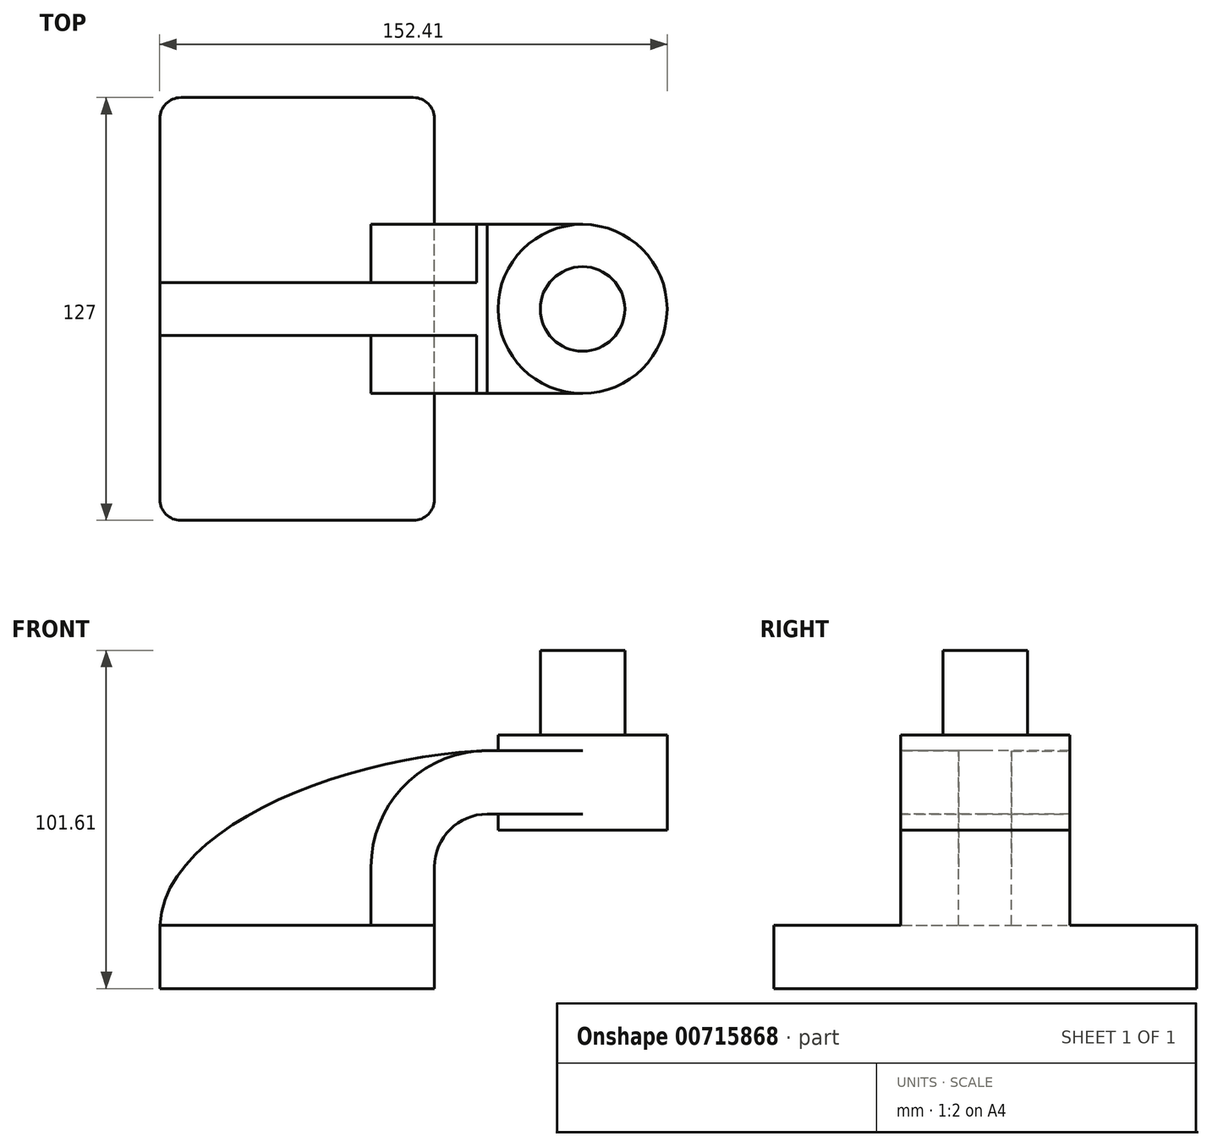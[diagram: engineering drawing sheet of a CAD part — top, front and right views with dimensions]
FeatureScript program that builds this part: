
annotation { "Feature Type Name" : "Feature", "Feature Type Description" : "" }
export const myFeature = defineFeature(function(context is Context, id is Id, definition is map)
    precondition{}
    {
        {
            var Q0;
            Q0=qCreatedBy(makeId("Front.planeOp"),FACE);
            var sketch = newSketch(context, id + "F0", { "sketchPlane" : qUnion([Q0])});
            skLineSegment(sketch, "E0.rect.bottom", {"start": v(-41.28, 9.52) * mm, "end": v(41.28, 9.52) * mm});
            skLineSegment(sketch, "E0.rect.top", {"start": v(-41.28, -9.52) * mm, "end": v(41.28, -9.52) * mm});
            skLineSegment(sketch, "E0.rect.left", {"start": v(-41.28, 9.52) * mm, "end": v(-41.28, -9.52) * mm});
            skLineSegment(sketch, "E0.rect.right", {"start": v(41.28, 9.52) * mm, "end": v(41.28, -9.52) * mm});
            skPoint(sketch, "E0.rect.middle", {"position": v(0, 0) * mm});
            skLineSegment(sketch, "E1", {"start": v(41.28, 9.52) * mm, "end": v(41.28, 27) * mm});
            skArc(sketch, "E2", {"start": v(41.28, 27) * mm, "mid": v(45.92, 38.23) * mm, "end": v(57.15, 42.88) * mm});
            skLineSegment(sketch, "E3", {"start": v(57.15, 42.88) * mm, "end": v(85.72, 42.88) * mm});
            skLineSegment(sketch, "E4.rect.bottom", {"start": v(60.32, 38.1) * mm, "end": v(111.12, 38.1) * mm});
            skLineSegment(sketch, "E4.rect.top", {"start": v(60.32, 66.68) * mm, "end": v(111.12, 66.68) * mm});
            skLineSegment(sketch, "E4.rect.left", {"start": v(60.32, 38.1) * mm, "end": v(60.32, 66.68) * mm});
            skLineSegment(sketch, "E4.rect.right", {"start": v(111.13, 38.1) * mm, "end": v(111.12, 66.68) * mm});
            skPoint(sketch, "E4.rect.middle", {"position": v(85.72, 52.39) * mm});
            skLineSegment(sketch, "E5.0", {"start": v(57.15, 61.93) * mm, "end": v(85.72, 61.93) * mm});
            skArc(sketch, "E5.1", {"start": v(22.23, 27) * mm, "mid": v(32.45, 51.7) * mm, "end": v(57.15, 61.93) * mm});
            skLineSegment(sketch, "E5.2", {"start": v(22.23, 9.52) * mm, "end": v(22.23, 27) * mm});
            skLineSegment(sketch, "E6", {"start": v(85.72, 38.1) * mm, "end": v(85.72, 66.68) * mm});
            skFitSpline(sketch, "E7", {"points": [v(-41.28, 9.53) * mm, v(57.15, 61.93) * mm], "startDerivative": vector(5.2, 92.34) * mm, "endDerivative": vector(120.92, 4.22) * mm});
            skSolve(sketch);
        }
        {
            var Q0;
            Q0=makeQuery(id+"F0.imprint","IMPRINT",FACE,{"disambiguationData":[TD([[makeQuery(id+"F0.imprint","IMPRINT",EDGE,{"derivedFrom":sQuery(id+"F0.wireOp",EDGE,"E0.rect.top")}),1.0]])]});
            extrude(context, id + "F1", {"entities" : qUnion([Q0]), "endBound" : BoundingType.SYMMETRIC, "depth" : 127 * mm});
        }
        {
            var Q0;
            {var subQ9=sQuery(id+"F0.wireOp",EDGE,"E1");Q0=makeQuery(id+"F0.imprint","IMPRINT",FACE,{"disambiguationData":[TD([[makeQuery(id+"F0.imprint","IMPRINT",EDGE,{"derivedFrom":subQ9}),1.0]])]});}
            var Q1;
            {var subQ0=sQuery(id+"F0.wireOp",EDGE,"E6");var subQ1=sQuery(id+"F0.wireOp",EDGE,"E3");var subQ2=makeQuery(id+"F0.imprint","INTERSECT",VERTEX,{"derivedFrom":[subQ1,subQ0]});Q1=makeQuery(id+"F0.imprint","IMPRINT",FACE,{"disambiguationData":[TD([[makeQuery(id+"F0.imprint","IMPRINT",EDGE,{"disambiguationData":[TD([[subQ2,1.0]])],"derivedFrom":subQ1}),1.0]])]});}
            extrude(context, id + "F2", {"entities" : qUnion([Q0, Q1]), "operationType" : NewBodyOperationType.ADD, "endBound" : BoundingType.SYMMETRIC, "depth" : 50.8 * mm});
        }
        {
            var Q0;
            {var subQ3=sQuery(id+"F0.wireOp",EDGE,"E5.2");Q0=makeQuery(id+"F0.imprint","IMPRINT",FACE,{"disambiguationData":[TD([[makeQuery(id+"F0.imprint","IMPRINT",EDGE,{"derivedFrom":subQ3}),1.0]])]});}
            extrude(context, id + "F3", {"entities" : qUnion([Q0]), "operationType" : NewBodyOperationType.ADD, "endBound" : BoundingType.SYMMETRIC, "depth" : 15.88 * mm});
        }
        {
            var Q0;
            {var subQ5=sQuery(id+"F0.wireOp",EDGE,"E4.rect.right");Q0=makeQuery(id+"F0.imprint","IMPRINT",FACE,{"disambiguationData":[TD([[makeQuery(id+"F0.imprint","IMPRINT",EDGE,{"derivedFrom":subQ5}),1.0]])]});}
            var Q1;
            Q1=sQuery(id+"F0.wireOp",EDGE,"E6");
            revolve(context, id + "F4", {"operationType" : NewBodyOperationType.ADD, "entities" : qUnion([Q0]), "axis" : qUnion([Q1]), "revolveType" : RevolveType.FULL});
        }
        {
            var Q0;
            Q0=makeQuery(id+"F1.opExtrude","CAP_EDGE",EDGE,{"disambiguationData":[OSD([sQuery(id+"F0.wireOp",EDGE,"E0.rect.right")])],"isStart":false});
            var Q1;
            Q1=makeQuery(id+"F1.opExtrude","CAP_EDGE",EDGE,{"disambiguationData":[OSD([sQuery(id+"F0.wireOp",EDGE,"E0.rect.left")])],"isStart":false});
            var Q2;
            Q2=makeQuery(id+"F1.opExtrude","CAP_EDGE",EDGE,{"disambiguationData":[OSD([sQuery(id+"F0.wireOp",EDGE,"E0.rect.right")])],"isStart":true});
            var Q3;
            Q3=makeQuery(id+"F1.opExtrude","CAP_EDGE",EDGE,{"disambiguationData":[OSD([sQuery(id+"F0.wireOp",EDGE,"E0.rect.left")])],"isStart":true});
            fillet(context, id + "F5", {"entities" : qUnion([Q0, Q1, Q2, Q3]), "radius" : 6.35 * mm, "tangentPropagation" : true, "allowEdgeOverflow" : false});
        }
        {
            var Q0;
            Q0=makeQuery(id+"F4.opRevolve","SWEPT_FACE",FACE,{"disambiguationData":[OSD([sQuery(id+"F0.wireOp",EDGE,"E4.rect.top")])]});
            var sketch = newSketch(context, id + "F6", { "sketchPlane" : qUnion([Q0])});
            skCircle(sketch, "E8", {"center": v(85.72, 0) * mm, "radius": 12.7 * mm});
            skSolve(sketch);
        }
        {
            var Q0;
            Q0=makeQuery(id+"F6.imprint","IMPRINT",FACE,{"disambiguationData":[TD([[makeQuery(id+"F6.imprint","IMPRINT",EDGE,{"derivedFrom":sQuery(id+"F6.wireOp",EDGE,"E8")}),1.0]])]});
            extrude(context, id + "F7", {"entities" : qUnion([Q0]), "operationType" : NewBodyOperationType.ADD, "depth" : 25.4 * mm, "offsetDistance" : 25.4 * mm});
        }
    });
